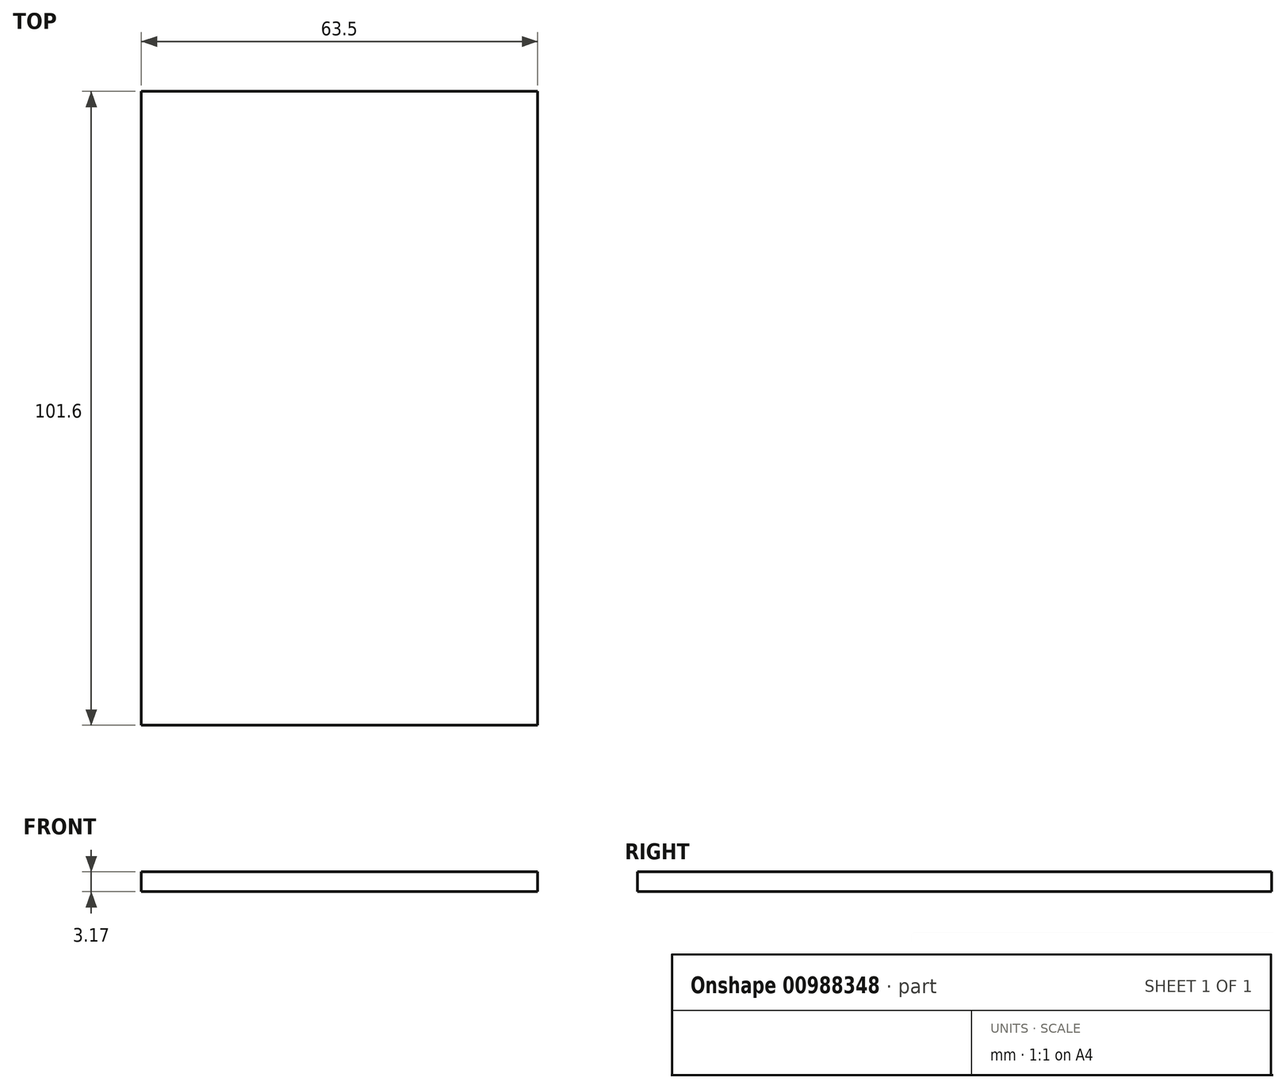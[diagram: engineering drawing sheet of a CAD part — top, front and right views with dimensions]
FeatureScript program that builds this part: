
annotation { "Feature Type Name" : "Feature", "Feature Type Description" : "" }
export const myFeature = defineFeature(function(context is Context, id is Id, definition is map)
    precondition{}
    {
        {
            var Q0;
            Q0=qCreatedBy(makeId("Top.planeOp"),FACE);
            var sketch = newSketch(context, id + "F0", { "sketchPlane" : qUnion([Q0])});
            skLineSegment(sketch, "E0.bottom", {"start": v(-31.75, 50.8) * mm, "end": v(31.75, 50.8) * mm});
            skLineSegment(sketch, "E0.top", {"start": v(-31.75, -50.8) * mm, "end": v(31.75, -50.8) * mm});
            skLineSegment(sketch, "E0.left", {"start": v(-31.75, 50.8) * mm, "end": v(-31.75, -50.8) * mm});
            skLineSegment(sketch, "E0.right", {"start": v(31.75, 50.8) * mm, "end": v(31.75, -50.8) * mm});
            skSolve(sketch);
        }
        {
            var Q0;
            Q0=makeQuery(id+"F0.imprint","IMPRINT",FACE,{"disambiguationData":[TD([[makeQuery(id+"F0.imprint","IMPRINT",EDGE,{"derivedFrom":sQuery(id+"F0.wireOp",EDGE,"E0.bottom")}),-1.0]])]});
            extrude(context, id + "F1", {"entities" : qUnion([Q0]), "depth" : 3.17 * mm, "offsetDistance" : 25.4 * mm});
        }
    });
